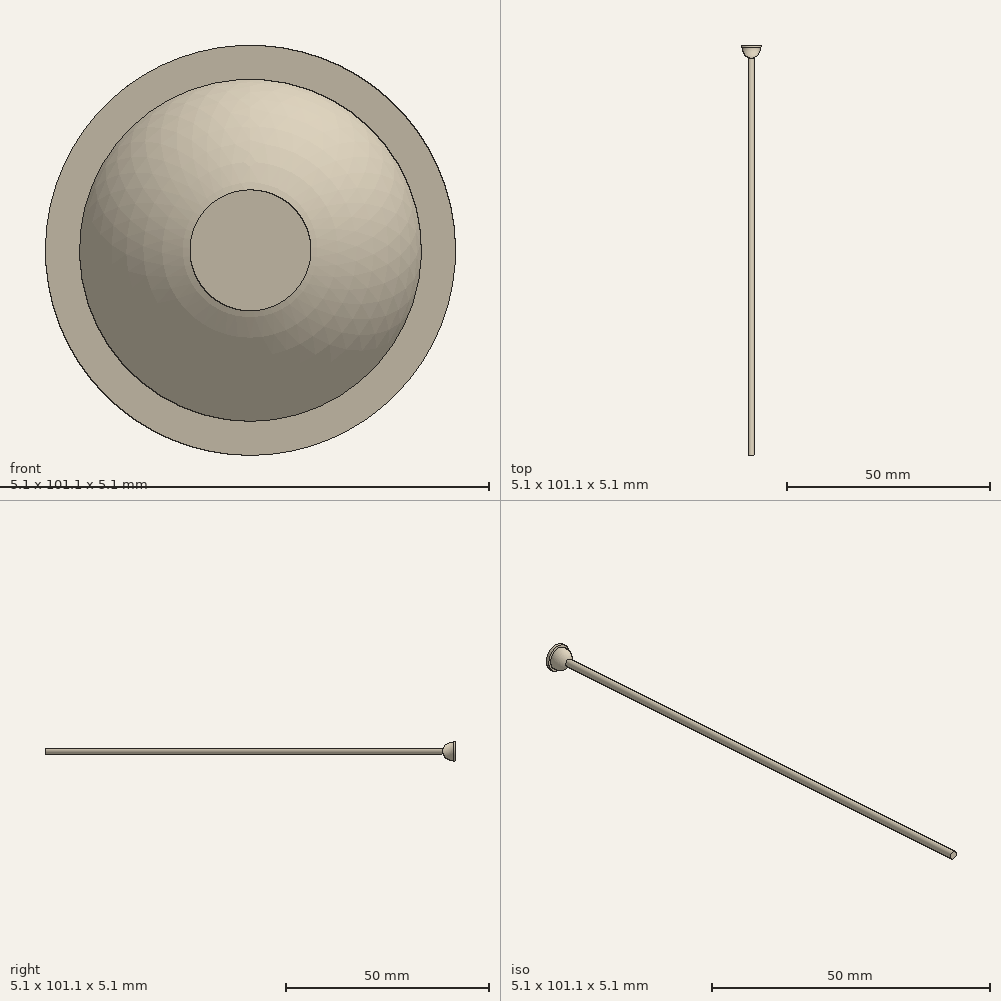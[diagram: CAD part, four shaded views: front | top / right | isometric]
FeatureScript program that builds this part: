
annotation { "Feature Type Name" : "Feature", "Feature Type Description" : "" }
export const myFeature = defineFeature(function(context is Context, id is Id, definition is map)
    precondition{}
    {
        {
            var Q0;
            Q0=qCreatedBy(makeId("Front.planeOp"),FACE);
            var sketch = newSketch(context, id + "F0", { "sketchPlane" : qUnion([Q0])});
            skCircle(sketch, "E0", {"center": v(0, 0) * mm, "radius": 0.76 * mm});
            skSolve(sketch);
        }
        {
            var Q0;
            Q0 = qSketchRegion(id + "F0", true);
            extrude(context, id + "F1", {"entities" : qUnion([Q0]), "depth" : 98 * mm});
        }
        {
            var Q0;
            Q0=qCreatedBy(makeId("Right.planeOp"),FACE);
            var sketch = newSketch(context, id + "F2", { "sketchPlane" : qUnion([Q0])});
            skLineSegment(sketch, "E1.0", {"start": v(3.12, 1.9) * mm, "end": v(3.12, 2.56) * mm});
            skArc(sketch, "E2", {"start": v(2.52, 2.1) * mm, "mid": v(0.77, 1.64) * mm, "end": v(0, 0) * mm});
            skLineSegment(sketch, "E3", {"start": v(3.12, 2.56) * mm, "end": v(2.52, 2.56) * mm});
            skLineSegment(sketch, "E4", {"start": v(2.52, 2.56) * mm, "end": v(2.52, 2.1) * mm});
            skLineSegment(sketch, "E5", {"start": v(3.12, 1.9) * mm, "end": v(3.12, 0) * mm});
            skLineSegment(sketch, "E6", {"start": v(0, 0) * mm, "end": v(3.12, 0) * mm});
            skSolve(sketch);
        }
        {
            var Q0;
            Q0=makeQuery(id+"F2.imprint","IMPRINT",FACE,{"disambiguationData":[TD([[makeQuery(id+"F2.imprint","IMPRINT",EDGE,{"derivedFrom":sQuery(id+"F2.wireOp",EDGE,"E1.0")}),1.0]])]});
            var Q1;
            Q1=sQuery(id+"F2.wireOp",EDGE,"E6");
            revolve(context, id + "F3", {"entities" : qUnion([Q0]), "axis" : qUnion([Q1]), "revolveType" : RevolveType.FULL});
        }
    });
